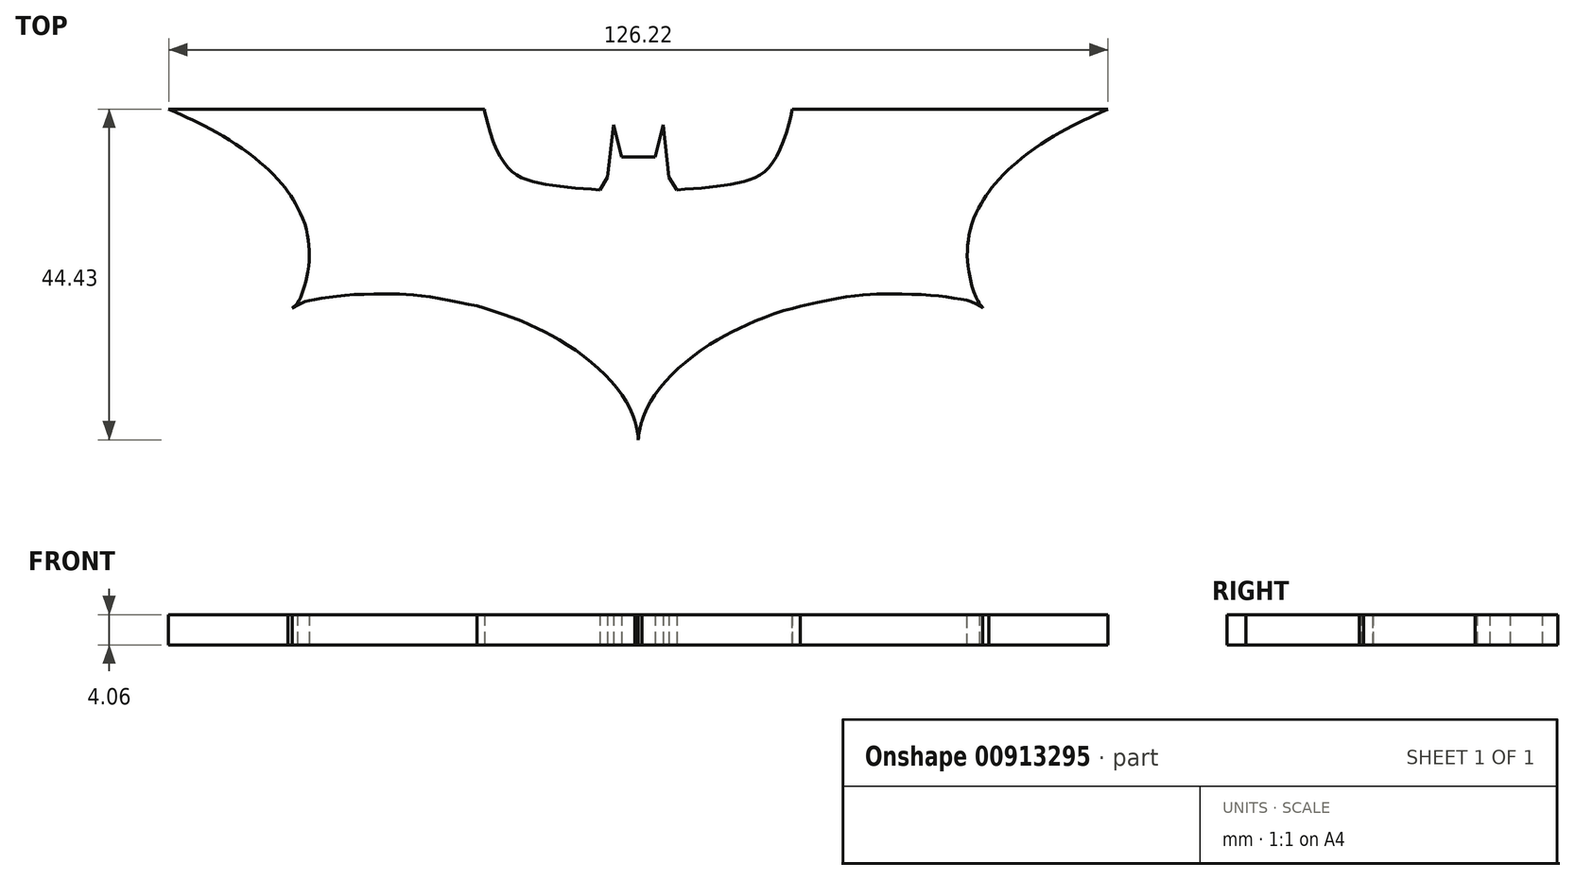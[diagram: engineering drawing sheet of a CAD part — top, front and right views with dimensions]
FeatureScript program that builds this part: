
annotation { "Feature Type Name" : "Feature", "Feature Type Description" : "" }
export const myFeature = defineFeature(function(context is Context, id is Id, definition is map)
    precondition{}
    {
        {
            var Q0;
            Q0=qCreatedBy(makeId("Top.planeOp"),FACE);
            var sketch = newSketch(context, id + "F0", { "sketchPlane" : qUnion([Q0])});
            skLineSegment(sketch, "E0", {"start": v(12.89, 49.73) * mm, "end": v(13.67, 42.63) * mm});
            skLineSegment(sketch, "E1", {"start": v(13.67, 42.63) * mm, "end": v(14.73, 40.96) * mm});
            skFitSpline(sketch, "E2", {"points": [v(14.73, 40.96) * mm, v(21.56, 41.64) * mm, v(25.73, 42.89) * mm, v(28.68, 46.6) * mm, v(30.2, 51.8) * mm, v(30.17, 51.8) * mm], "startDerivative": vector(25.75, 1.96) * mm, "endDerivative": vector(-1.88, -0.87) * mm});
            skLineSegment(sketch, "E3", {"start": v(30.2, 51.8) * mm, "end": v(72.65, 51.8) * mm});
            skFitSpline(sketch, "E4", {"points": [v(72.65, 51.8) * mm, v(71.84, 51.43) * mm, v(70.07, 50.65) * mm, v(68.15, 49.73) * mm, v(65.7, 48.4) * mm, v(63.07, 46.74) * mm, v(60.47, 44.75) * mm, v(59.02, 43.5) * mm, v(57.56, 41.9) * mm, v(56.6, 40.7) * mm], "startDerivative": vector(-10.09, -4.78) * mm, "endDerivative": vector(-9.4, -12.08) * mm});
            skFitSpline(sketch, "E5", {"points": [v(56.6, 40.7) * mm, v(55.88, 39.58) * mm, v(55.1, 38.16) * mm, v(54.33, 36.34) * mm, v(53.91, 34.47) * mm, v(53.75, 32.85) * mm, v(53.79, 31.2) * mm, v(54.05, 29.44) * mm, v(54.36, 28.05) * mm, v(55.06, 26.21) * mm, v(55.34, 25.69) * mm], "startDerivative": vector(-7.84, -11.86) * mm, "endDerivative": vector(4.06, -6.86) * mm});
            skFitSpline(sketch, "E6", {"points": [v(55.34, 25.69) * mm, v(56.02, 25.06) * mm], "startDerivative": vector(1.06, -1.17) * mm, "endDerivative": vector(0.1, 0.23) * mm});
            skFitSpline(sketch, "E7", {"points": [v(56.02, 25.06) * mm, v(54.27, 25.96) * mm, v(53.52, 26.16) * mm, v(51.7, 26.45) * mm, v(49.32, 26.76) * mm, v(45.83, 26.95) * mm, v(42.45, 26.95) * mm, v(40.58, 26.92) * mm, v(38.13, 26.68) * mm, v(34.37, 26.02) * mm, v(31.3, 25.3) * mm], "startDerivative": vector(-21.85, 12.06) * mm, "endDerivative": vector(-26.21, -5.76) * mm});
            skFitSpline(sketch, "E8", {"points": [v(31.3, 25.3) * mm, v(29.42, 24.83) * mm, v(26.77, 23.93) * mm, v(24.59, 23.04) * mm, v(22.8, 22.2) * mm, v(21.22, 21.39) * mm, v(19.42, 20.36) * mm, v(17.18, 18.84) * mm, v(15.24, 17.28) * mm, v(13.66, 15.74) * mm, v(12.26, 14.1) * mm, v(11.23, 12.58) * mm, v(10.42, 11) * mm, v(10, 9.92) * mm, v(10, 9.9) * mm], "startDerivative": vector(-23.61, -6.49) * mm, "endDerivative": vector(0.45, -1.73) * mm});
            skFitSpline(sketch, "E9", {"points": [v(10, 9.9) * mm, v(9.81, 9.13) * mm, v(9.6, 8.12) * mm, v(9.54, 7.37) * mm], "startDerivative": vector(-0.57, -2.28) * mm, "endDerivative": vector(-0.15, -2.27) * mm});
            skLineSegment(sketch, "E10", {"start": v(12.89, 49.73) * mm, "end": v(11.78, 45.36) * mm});
            skLineSegment(sketch, "E11", {"start": v(11.78, 45.36) * mm, "end": v(9.63, 45.36) * mm});
            skLineSegment(sketch, "E12", {"start": v(9.63, 45.36) * mm, "end": v(9.54, 45.36) * mm});
            skFitSpline(sketch, "E13.MirrorCS", {"points": [v(9.08, 9.9) * mm, v(9.26, 9.13) * mm, v(9.47, 8.12) * mm, v(9.54, 7.37) * mm], "startDerivative": vector(0.57, -2.28) * mm, "endDerivative": vector(0.15, -2.27) * mm});
            skFitSpline(sketch, "E14.MirrorCS", {"points": [v(-12.17, 25.36) * mm, v(-10.34, 24.83) * mm, v(-7.7, 23.93) * mm, v(-5.51, 23.04) * mm, v(-3.73, 22.2) * mm, v(-2.15, 21.39) * mm, v(-0.35, 20.36) * mm, v(1.9, 18.84) * mm, v(3.84, 17.28) * mm, v(5.42, 15.74) * mm, v(6.81, 14.1) * mm, v(7.84, 12.58) * mm, v(8.66, 11) * mm, v(9.08, 9.92) * mm, v(9.08, 9.9) * mm], "startDerivative": vector(23.61, -6.49) * mm, "endDerivative": vector(-0.45, -1.73) * mm});
            skFitSpline(sketch, "E15.MirrorCS", {"points": [v(-36.95, 25.06) * mm, v(-35.2, 25.96) * mm, v(-34.44, 26.16) * mm, v(-32.62, 26.45) * mm, v(-30.24, 26.76) * mm, v(-26.76, 26.95) * mm, v(-23.37, 26.95) * mm, v(-21.5, 26.92) * mm, v(-19.06, 26.68) * mm, v(-15.3, 26.02) * mm, v(-12.17, 25.36) * mm], "startDerivative": vector(21.85, 12.06) * mm, "endDerivative": vector(26.21, -5.76) * mm});
            skFitSpline(sketch, "E16.MirrorCS", {"points": [v(-37.52, 40.7) * mm, v(-36.8, 39.58) * mm, v(-36.03, 38.16) * mm, v(-35.26, 36.34) * mm, v(-34.84, 34.47) * mm, v(-34.67, 32.85) * mm, v(-34.7, 31.2) * mm, v(-34.97, 29.44) * mm, v(-35.29, 28.05) * mm, v(-35.98, 26.21) * mm, v(-36.26, 25.69) * mm], "startDerivative": vector(7.84, -11.86) * mm, "endDerivative": vector(-4.06, -6.86) * mm});
            skFitSpline(sketch, "E17.MirrorCS", {"points": [v(-53.57, 51.8) * mm, v(-52.76, 51.43) * mm, v(-51, 50.65) * mm, v(-49.07, 49.73) * mm, v(-46.63, 48.4) * mm, v(-44, 46.74) * mm, v(-41.4, 44.75) * mm, v(-39.95, 43.5) * mm, v(-38.48, 41.9) * mm, v(-37.52, 40.7) * mm], "startDerivative": vector(10.09, -4.78) * mm, "endDerivative": vector(9.4, -12.08) * mm});
            skLineSegment(sketch, "E18.MirrorCS", {"start": v(-11.13, 51.8) * mm, "end": v(-53.57, 51.8) * mm});
            skFitSpline(sketch, "E19.MirrorCS", {"points": [v(4.34, 40.96) * mm, v(-2.49, 41.64) * mm, v(-6.65, 42.89) * mm, v(-9.6, 46.6) * mm, v(-11.13, 51.8) * mm, v(-11.1, 51.8) * mm], "startDerivative": vector(-25.75, 1.96) * mm, "endDerivative": vector(1.88, -0.87) * mm});
            skLineSegment(sketch, "E20.MirrorCS", {"start": v(5.4, 42.63) * mm, "end": v(4.34, 40.96) * mm});
            skLineSegment(sketch, "E21.MirrorCS", {"start": v(6.19, 49.73) * mm, "end": v(5.4, 42.63) * mm});
            skLineSegment(sketch, "E22.MirrorCS", {"start": v(7.3, 45.36) * mm, "end": v(9.45, 45.36) * mm});
            skLineSegment(sketch, "E23.MirrorCS", {"start": v(6.19, 49.73) * mm, "end": v(7.3, 45.36) * mm});
            skLineSegment(sketch, "E24", {"start": v(9.45, 45.36) * mm, "end": v(9.54, 45.36) * mm});
            skLineSegment(sketch, "E25", {"start": v(-36.26, 25.69) * mm, "end": v(-36.95, 25.06) * mm});
            skSolve(sketch);
        }
        {
            var Q0;
            Q0=makeQuery(id+"F0.imprint","IMPRINT",FACE,{"disambiguationData":[TD([[makeQuery(id+"F0.imprint","IMPRINT",EDGE,{"derivedFrom":sQuery(id+"F0.wireOp",EDGE,"E0")}),-1.0]])]});
            extrude(context, id + "F1", {"entities" : qUnion([Q0]), "depth" : 4.06 * mm, "offsetDistance" : 25.4 * mm});
        }
    });
